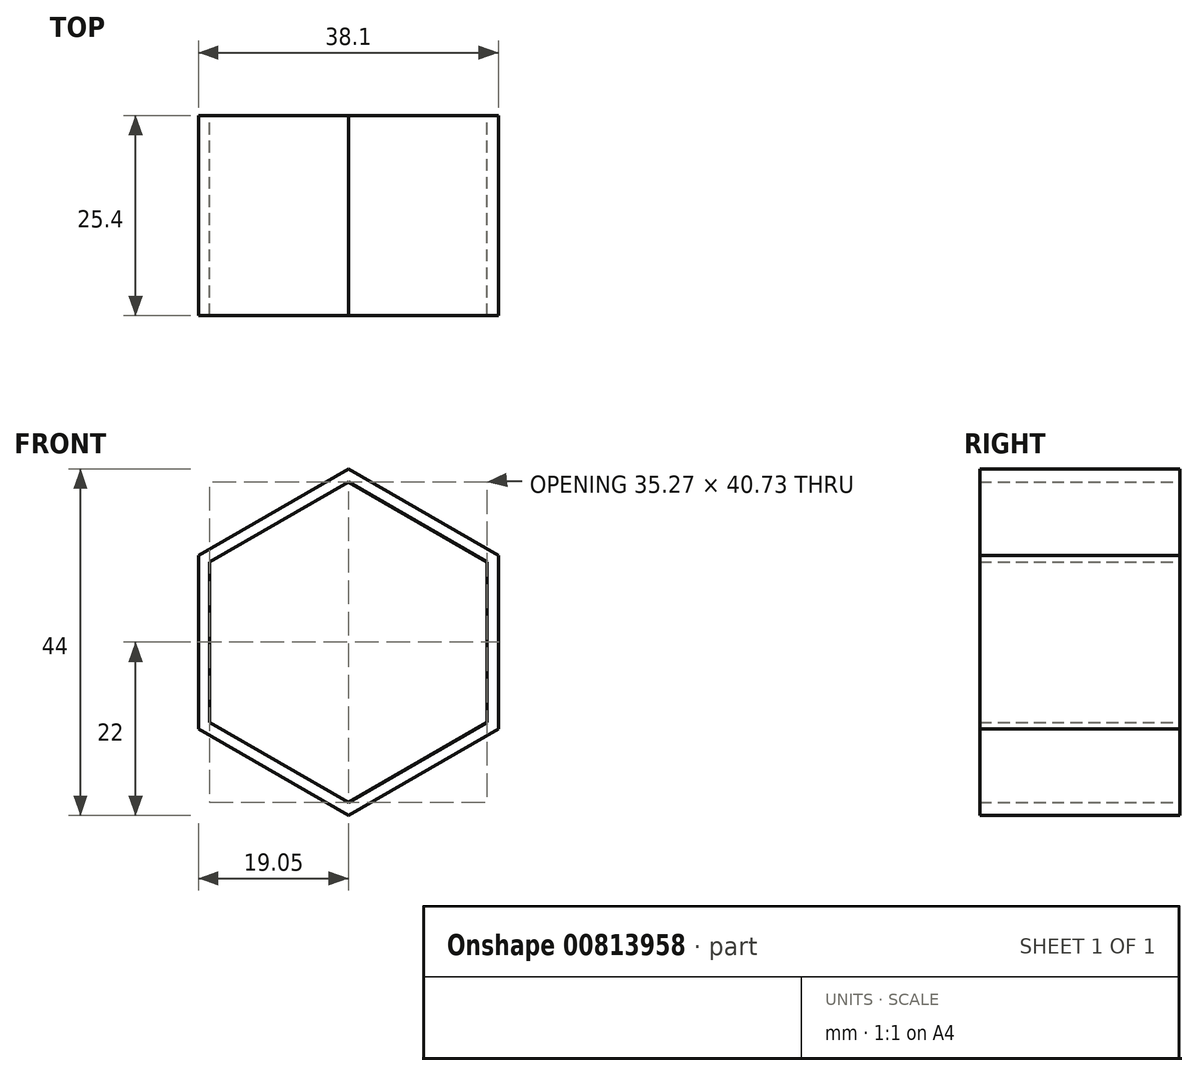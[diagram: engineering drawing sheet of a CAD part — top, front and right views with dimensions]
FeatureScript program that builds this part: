
annotation { "Feature Type Name" : "Feature", "Feature Type Description" : "" }
export const myFeature = defineFeature(function(context is Context, id is Id, definition is map)
    precondition{}
    {
        {
            var Q0;
            Q0=qCreatedBy(makeId("Front.planeOp"),FACE);
            var sketch = newSketch(context, id + "F0", { "sketchPlane" : qUnion([Q0])});
            skArc(sketch, "E0", {"start": v(-2.58, 18.87) * mm, "mid": v(-9.53, 16.5) * mm, "end": v(-15.06, 11.67) * mm});
            skPoint(sketch, "E1", {"position": v(-19.05, 0) * mm});
            skPoint(sketch, "E2", {"position": v(19.05, 0) * mm});
            skPoint(sketch, "E3", {"position": v(0, -19.05) * mm});
            skPoint(sketch, "E4", {"position": v(0, 19.05) * mm});
            skArc(sketch, "E5.cCircle", {"start": v(15.06, 11.67) * mm, "mid": v(9.52, 16.5) * mm, "end": v(2.58, 18.87) * mm, "construction": true});
            skLineSegment(sketch, "E5.0", {"start": v(-19.05, -11) * mm, "end": v(-19.05, 11) * mm});
            skLineSegment(sketch, "E5.1", {"start": v(-19.05, 11) * mm, "end": v(0, 22) * mm});
            skLineSegment(sketch, "E5.2", {"start": v(0, 22) * mm, "end": v(19.05, 11) * mm});
            skLineSegment(sketch, "E5.3", {"start": v(19.05, 11) * mm, "end": v(19.05, -11) * mm});
            skLineSegment(sketch, "E5.4", {"start": v(19.05, -11) * mm, "end": v(0, -22) * mm});
            skLineSegment(sketch, "E5.5", {"start": v(0, -22) * mm, "end": v(-19.05, -11) * mm});
            skLineSegment(sketch, "E6.0", {"start": v(-17.64, -10.18) * mm, "end": v(-17.64, 10.18) * mm});
            skLineSegment(sketch, "E6.1", {"start": v(-17.64, 10.18) * mm, "end": v(0, 20.36) * mm});
            skLineSegment(sketch, "E6.2", {"start": v(0, 20.36) * mm, "end": v(17.64, 10.18) * mm});
            skLineSegment(sketch, "E6.3", {"start": v(17.64, 10.18) * mm, "end": v(17.64, -10.18) * mm});
            skLineSegment(sketch, "E6.4", {"start": v(17.64, -10.18) * mm, "end": v(0, -20.36) * mm});
            skLineSegment(sketch, "E6.5", {"start": v(0, -20.36) * mm, "end": v(-17.64, -10.18) * mm});
            skPoint(sketch, "E6.0.midPoint", {"position": v(-17.64, 0) * mm});
            skArc(sketch, "E7.trimOffspring", {"start": v(-2.58, 18.87) * mm, "mid": v(-9.53, 16.5) * mm, "end": v(-15.06, 11.67) * mm, "construction": true});
            skArc(sketch, "E8.trimOffspring", {"start": v(2.58, -18.87) * mm, "mid": v(9.53, -16.5) * mm, "end": v(15.06, -11.67) * mm, "construction": true});
            skArc(sketch, "E9.trimOffspring", {"start": v(2.58, -18.87) * mm, "mid": v(9.53, -16.5) * mm, "end": v(15.06, -11.67) * mm});
            skArc(sketch, "E10.trimOffspring", {"start": v(-17.64, 7.2) * mm, "mid": v(-19.05, 0) * mm, "end": v(-17.64, -7.2) * mm, "construction": true});
            skArc(sketch, "E11.trimOffspring", {"start": v(-15.06, -11.67) * mm, "mid": v(-9.52, -16.5) * mm, "end": v(-2.58, -18.87) * mm, "construction": true});
            skArc(sketch, "E12.trimOffspring", {"start": v(-17.64, 7.2) * mm, "mid": v(-19.05, 0) * mm, "end": v(-17.64, -7.2) * mm});
            skArc(sketch, "E13.trimOffspring", {"start": v(-15.06, -11.67) * mm, "mid": v(-9.52, -16.5) * mm, "end": v(-2.58, -18.87) * mm});
            skArc(sketch, "E14.trimOffspring", {"start": v(17.64, -7.2) * mm, "mid": v(19.05, 0) * mm, "end": v(17.64, 7.2) * mm, "construction": true});
            skArc(sketch, "E15.trimOffspring", {"start": v(17.64, -7.2) * mm, "mid": v(19.05, 0) * mm, "end": v(17.64, 7.2) * mm});
            skArc(sketch, "E16.trimOffspring", {"start": v(15.06, 11.67) * mm, "mid": v(9.52, 16.5) * mm, "end": v(2.58, 18.87) * mm});
            skSolve(sketch);
        }
        {
            var Q0;
            Q0 = qSketchRegion(id + "F0", true);
            extrude(context, id + "F1", {"entities" : qUnion([Q0]), "depth" : 25.4 * mm, "offsetDistance" : 25.4 * mm});
        }
    });
